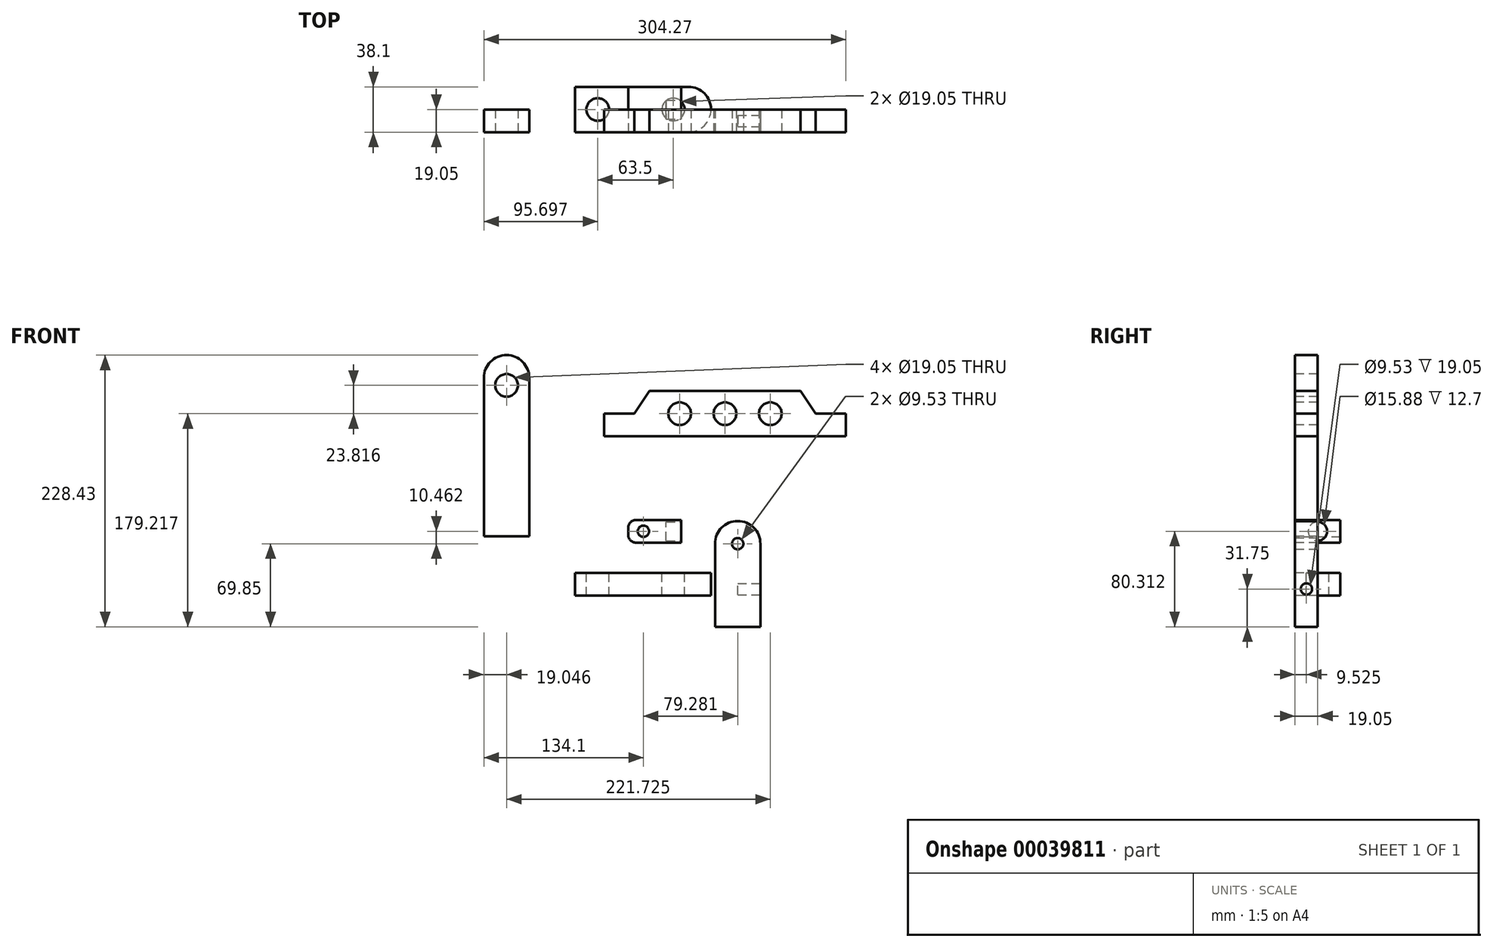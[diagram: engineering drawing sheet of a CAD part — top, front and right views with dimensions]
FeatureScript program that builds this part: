
annotation { "Feature Type Name" : "Feature", "Feature Type Description" : "" }
export const myFeature = defineFeature(function(context is Context, id is Id, definition is map)
    precondition{}
    {
        {
            var Q0;
            Q0=qCreatedBy(makeId("Front.planeOp"),FACE);
            var sketch = newSketch(context, id + "F0", { "sketchPlane" : qUnion([Q0])});
            skLineSegment(sketch, "E0.bottom", {"start": v(-26.75, 15.88) * mm, "end": v(17.7, 15.88) * mm});
            skLineSegment(sketch, "E0.top", {"start": v(-26.75, 34.93) * mm, "end": v(17.7, 34.93) * mm});
            skLineSegment(sketch, "E0.left", {"start": v(-26.75, 15.88) * mm, "end": v(-26.75, 34.93) * mm});
            skLineSegment(sketch, "E0.right", {"start": v(17.7, 15.88) * mm, "end": v(17.7, 34.93) * mm});
            skSolve(sketch);
        }
        {
            var Q0;
            Q0=makeQuery(id+"F0.imprint","IMPRINT",FACE,{"disambiguationData":[TD([[makeQuery(id+"F0.imprint","IMPRINT",EDGE,{"derivedFrom":sQuery(id+"F0.wireOp",EDGE,"E0.bottom")}),1.0]])]});
            extrude(context, id + "F1", {"entities" : qUnion([Q0]), "oppositeDirection" : true, "depth" : 38.1 * mm});
        }
        {
            var Q0;
            Q0=makeQuery(id+"F1.opExtrude","CAP_FACE",FACE,{"disambiguationData":[OSD([sQuery(id+"F0.wireOp",EDGE,"E0.bottom"),sQuery(id+"F0.wireOp",EDGE,"E0.top"),sQuery(id+"F0.wireOp",EDGE,"E0.left"),sQuery(id+"F0.wireOp",EDGE,"E0.right")])],"isStart":true});
            var sketch = newSketch(context, id + "F2", { "sketchPlane" : qUnion([Q0])});
            skCircle(sketch, "E1", {"center": v(-14.05, 25.4) * mm, "radius": 4.76 * mm});
            skPoint(sketch, "E2.orphan", {"position": v(17.7, 25.4) * mm});
            skPoint(sketch, "E3.start.orphan", {"position": v(-26.75, 25.4) * mm});
            skSolve(sketch);
        }
        {
            var Q0;
            Q0=makeQuery(id+"F2.imprint","IMPRINT",FACE,{"disambiguationData":[TD([[makeQuery(id+"F2.imprint","IMPRINT",EDGE,{"derivedFrom":sQuery(id+"F2.wireOp",EDGE,"E1")}),1.0]])]});
            extrude(context, id + "F3", {"entities" : qUnion([Q0]), "operationType" : NewBodyOperationType.REMOVE, "oppositeDirection" : true, "depth" : 118.58 * mm});
        }
        {
            var Q0;
            Q0=makeQuery(id+"F1.opExtrude","SWEPT_FACE",FACE,{"disambiguationData":[OSD([sQuery(id+"F0.wireOp",EDGE,"E0.right")])]});
            var sketch = newSketch(context, id + "F4", { "sketchPlane" : qUnion([Q0])});
            skCircle(sketch, "E4", {"center": v(19.05, 25.4) * mm, "radius": 7.94 * mm});
            skSolve(sketch);
        }
        {
            var Q0;
            Q0=makeQuery(id+"F4.imprint","IMPRINT",FACE,{"disambiguationData":[TD([[makeQuery(id+"F4.imprint","IMPRINT",EDGE,{"derivedFrom":sQuery(id+"F4.wireOp",EDGE,"E4")}),1.0]])]});
            extrude(context, id + "F5", {"entities" : qUnion([Q0]), "operationType" : NewBodyOperationType.REMOVE, "oppositeDirection" : true, "depth" : 12.7 * mm});
        }
        {
            var Q0;
            Q0=makeQuery(id+"F1.opExtrude","SWEPT_EDGE",EDGE,{"disambiguationData":[OSD([sQuery(id+"F0.wireOp",EDGE,"E0.top"),sQuery(id+"F0.wireOp",EDGE,"E0.left")])]});
            var Q1;
            Q1=makeQuery(id+"F1.opExtrude","SWEPT_EDGE",EDGE,{"disambiguationData":[OSD([sQuery(id+"F0.wireOp",EDGE,"E0.bottom"),sQuery(id+"F0.wireOp",EDGE,"E0.left")])]});
            fillet(context, id + "F6", {"entities" : qUnion([Q0, Q1]), "radius" : 6.35 * mm, "tangentPropagation" : true, "allowEdgeOverflow" : false});
        }
        {
            var Q0;
            Q0=qCreatedBy(makeId("Front.planeOp"),FACE);
            var sketch = newSketch(context, id + "F7", { "sketchPlane" : qUnion([Q0])});
            skLineSegment(sketch, "E5.bottom", {"start": v(46.18, 34) * mm, "end": v(84.28, 34) * mm});
            skLineSegment(sketch, "E5.top", {"start": v(46.18, -54.9) * mm, "end": v(84.28, -54.9) * mm});
            skLineSegment(sketch, "E5.left", {"start": v(46.18, 34) * mm, "end": v(46.18, -54.9) * mm});
            skLineSegment(sketch, "E5.right", {"start": v(84.28, 34) * mm, "end": v(84.28, -54.9) * mm});
            skCircle(sketch, "E6", {"center": v(65.23, 14.94) * mm, "radius": 4.76 * mm});
            skSolve(sketch);
        }
        {
            var Q0;
            Q0=makeQuery(id+"F7.imprint","IMPRINT",FACE,{"disambiguationData":[TD([[makeQuery(id+"F7.imprint","IMPRINT",EDGE,{"derivedFrom":sQuery(id+"F7.wireOp",EDGE,"E5.bottom")}),-1.0]])]});
            extrude(context, id + "F8", {"entities" : qUnion([Q0]), "oppositeDirection" : true, "depth" : 19.05 * mm});
        }
        {
            var Q0;
            Q0=makeQuery(id+"F8.opExtrude","SWEPT_FACE",FACE,{"disambiguationData":[OSD([sQuery(id+"F7.wireOp",EDGE,"E5.right")])]});
            var sketch = newSketch(context, id + "F9", { "sketchPlane" : qUnion([Q0])});
            skCircle(sketch, "E7", {"center": v(9.53, -23.16) * mm, "radius": 4.76 * mm});
            skSolve(sketch);
        }
        {
            var Q0;
            Q0=makeQuery(id+"F9.imprint","IMPRINT",FACE,{"disambiguationData":[TD([[makeQuery(id+"F9.imprint","IMPRINT",EDGE,{"derivedFrom":sQuery(id+"F9.wireOp",EDGE,"E7")}),1.0]])]});
            extrude(context, id + "F10", {"entities" : qUnion([Q0]), "operationType" : NewBodyOperationType.REMOVE, "oppositeDirection" : true, "depth" : 19.05 * mm});
        }
        {
            var Q0;
            Q0=makeQuery(id+"F8.opExtrude","SWEPT_EDGE",EDGE,{"disambiguationData":[OSD([sQuery(id+"F7.wireOp",EDGE,"E5.bottom"),sQuery(id+"F7.wireOp",EDGE,"E5.right")])]});
            var Q1;
            Q1=makeQuery(id+"F8.opExtrude","SWEPT_EDGE",EDGE,{"disambiguationData":[OSD([sQuery(id+"F7.wireOp",EDGE,"E5.bottom"),sQuery(id+"F7.wireOp",EDGE,"E5.left")])]});
            fillet(context, id + "F11", {"entities" : qUnion([Q0, Q1]), "radius" : 19.05 * mm, "tangentPropagation" : true, "allowEdgeOverflow" : false});
        }
        {
            var Q0;
            Q0=qCreatedBy(makeId("Front.planeOp"),FACE);
            var sketch = newSketch(context, id + "F12", { "sketchPlane" : qUnion([Q0])});
            skLineSegment(sketch, "E8.bottom", {"start": v(-71.5, -9.7) * mm, "end": v(42.8, -9.7) * mm});
            skLineSegment(sketch, "E8.top", {"start": v(-71.5, -28.76) * mm, "end": v(42.8, -28.76) * mm});
            skLineSegment(sketch, "E8.left", {"start": v(-71.5, -9.7) * mm, "end": v(-71.5, -28.76) * mm});
            skLineSegment(sketch, "E8.right", {"start": v(42.8, -9.7) * mm, "end": v(42.8, -28.76) * mm});
            skSolve(sketch);
        }
        {
            var Q0;
            Q0=makeQuery(id+"F12.imprint","IMPRINT",FACE,{"disambiguationData":[TD([[makeQuery(id+"F12.imprint","IMPRINT",EDGE,{"derivedFrom":sQuery(id+"F12.wireOp",EDGE,"E8.bottom")}),-1.0]])]});
            extrude(context, id + "F13", {"entities" : qUnion([Q0]), "oppositeDirection" : true, "depth" : 38.1 * mm});
        }
        {
            var Q0;
            Q0=makeQuery(id+"F13.opExtrude","SWEPT_FACE",FACE,{"disambiguationData":[OSD([sQuery(id+"F12.wireOp",EDGE,"E8.bottom")])]});
            var sketch = newSketch(context, id + "F14", { "sketchPlane" : qUnion([Q0])});
            skCircle(sketch, "E9", {"center": v(-52.45, 19.05) * mm, "radius": 9.53 * mm});
            skCircle(sketch, "E10", {"center": v(11.05, 19.05) * mm, "radius": 9.53 * mm});
            skSolve(sketch);
        }
        {
            var Q0;
            Q0=makeQuery(id+"F14.imprint","IMPRINT",FACE,{"disambiguationData":[TD([[makeQuery(id+"F14.imprint","IMPRINT",EDGE,{"derivedFrom":sQuery(id+"F14.wireOp",EDGE,"E9")}),1.0]])]});
            var Q1;
            Q1=makeQuery(id+"F14.imprint","IMPRINT",FACE,{"disambiguationData":[TD([[makeQuery(id+"F14.imprint","IMPRINT",EDGE,{"derivedFrom":sQuery(id+"F14.wireOp",EDGE,"E10")}),1.0]])]});
            extrude(context, id + "F15", {"entities" : qUnion([Q0, Q1]), "operationType" : NewBodyOperationType.REMOVE, "oppositeDirection" : true, "depth" : 43.38 * mm});
        }
        {
            var Q0;
            Q0=makeQuery(id+"F13.opExtrude","CAP_EDGE",EDGE,{"disambiguationData":[OSD([sQuery(id+"F12.wireOp",EDGE,"E8.right")])],"isStart":false});
            var Q1;
            Q1=makeQuery(id+"F13.opExtrude","CAP_EDGE",EDGE,{"disambiguationData":[OSD([sQuery(id+"F12.wireOp",EDGE,"E8.right")])],"isStart":true});
            fillet(context, id + "F16", {"entities" : qUnion([Q0, Q1]), "radius" : 19.05 * mm, "tangentPropagation" : true, "allowEdgeOverflow" : false});
        }
        {
            var Q0;
            Q0=qCreatedBy(makeId("Front.planeOp"),FACE);
            var sketch = newSketch(context, id + "F17", { "sketchPlane" : qUnion([Q0])});
            skLineSegment(sketch, "E11.bottom", {"start": v(-129.1, 173.52) * mm, "end": v(-129.1, 173.52) * mm});
            skLineSegment(sketch, "E11.top", {"start": v(-148.15, 21.12) * mm, "end": v(-110.05, 21.12) * mm});
            skLineSegment(sketch, "E11.left", {"start": v(-148.15, 154.47) * mm, "end": v(-148.15, 21.12) * mm});
            skLineSegment(sketch, "E11.right", {"start": v(-110.05, 154.47) * mm, "end": v(-110.05, 21.12) * mm});
            skCircle(sketch, "E12", {"center": v(-129.1, 148.12) * mm, "radius": 9.53 * mm});
            skPoint(sketch, "E13.visualSharp", {"position": v(-148.15, 173.52) * mm});
            skArc(sketch, "E13.filletArc", {"start": v(-129.1, 173.52) * mm, "mid": v(-142.57, 167.94) * mm, "end": v(-148.15, 154.47) * mm});
            skPoint(sketch, "E14.visualSharp", {"position": v(-110.05, 173.52) * mm});
            skArc(sketch, "E14.filletArc", {"start": v(-110.05, 154.47) * mm, "mid": v(-115.63, 167.94) * mm, "end": v(-129.1, 173.52) * mm});
            skSolve(sketch);
        }
        {
            var Q0;
            Q0=makeQuery(id+"F17.imprint","IMPRINT",FACE,{"disambiguationData":[TD([[makeQuery(id+"F17.imprint","IMPRINT",EDGE,{"derivedFrom":sQuery(id+"F17.wireOp",EDGE,"E11.top")}),1.0]])]});
            extrude(context, id + "F18", {"entities" : qUnion([Q0]), "oppositeDirection" : true, "depth" : 19.05 * mm});
        }
        {
            var Q0;
            Q0=qCreatedBy(makeId("Front.planeOp"),FACE);
            var sketch = newSketch(context, id + "F19", { "sketchPlane" : qUnion([Q0])});
            skLineSegment(sketch, "E15.bottom", {"start": v(-8.98, 143.36) * mm, "end": v(118.02, 143.36) * mm});
            skLineSegment(sketch, "E15.top", {"start": v(-47.08, 105.26) * mm, "end": v(156.12, 105.26) * mm});
            skLineSegment(sketch, "E15.left", {"start": v(-47.08, 124.3) * mm, "end": v(-47.08, 105.26) * mm});
            skLineSegment(sketch, "E15.right", {"start": v(156.12, 124.3) * mm, "end": v(156.12, 105.26) * mm});
            skLineSegment(sketch, "E16", {"start": v(-47.08, 124.3) * mm, "end": v(-21.68, 124.3) * mm});
            skLineSegment(sketch, "E17", {"start": v(-21.68, 124.3) * mm, "end": v(-8.98, 143.36) * mm});
            skCircle(sketch, "E18", {"center": v(16.42, 124.3) * mm, "radius": 9.53 * mm});
            skCircle(sketch, "E19", {"center": v(54.52, 124.3) * mm, "radius": 9.53 * mm});
            skPoint(sketch, "E20.orphan", {"position": v(-47.08, 143.36) * mm});
            skLineSegment(sketch, "E21.MirrorCS", {"start": v(130.72, 124.3) * mm, "end": v(118.02, 143.36) * mm});
            skLineSegment(sketch, "E22.MirrorCS", {"start": v(156.12, 124.3) * mm, "end": v(130.72, 124.3) * mm});
            skPoint(sketch, "E23.orphan", {"position": v(156.12, 143.36) * mm});
            skCircle(sketch, "E24.MirrorC", {"center": v(92.62, 124.3) * mm, "radius": 9.53 * mm});
            skPoint(sketch, "E25.orphan", {"position": v(54.52, 143.36) * mm});
            skPoint(sketch, "E26.orphan", {"position": v(54.52, 105.26) * mm});
            skSolve(sketch);
        }
        {
            var Q0;
            Q0=makeQuery(id+"F19.imprint","IMPRINT",FACE,{"disambiguationData":[TD([[makeQuery(id+"F19.imprint","IMPRINT",EDGE,{"derivedFrom":sQuery(id+"F19.wireOp",EDGE,"E15.bottom")}),-1.0]])]});
            extrude(context, id + "F20", {"entities" : qUnion([Q0]), "oppositeDirection" : true, "depth" : 19.05 * mm});
        }
    });
